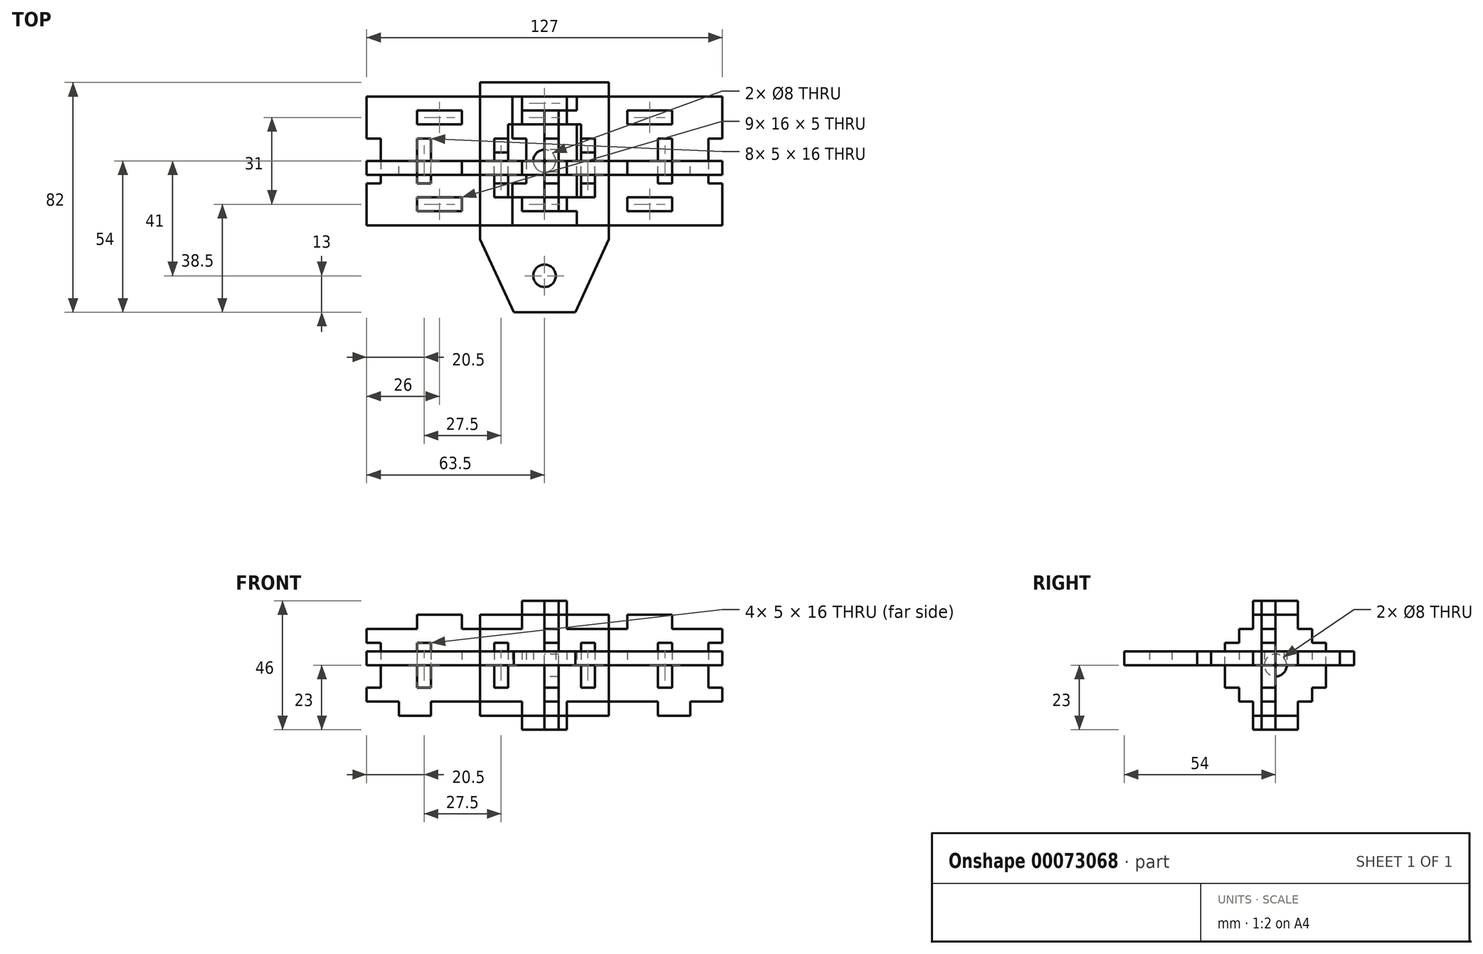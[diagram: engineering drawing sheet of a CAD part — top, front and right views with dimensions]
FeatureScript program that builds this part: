
annotation { "Feature Type Name" : "Feature", "Feature Type Description" : "" }
export const myFeature = defineFeature(function(context is Context, id is Id, definition is map)
    precondition{}
    {
        {
            var Q0;
            Q0=qCreatedBy(makeId("Top.planeOp"),FACE);
            var sketch = newSketch(context, id + "F0", { "sketchPlane" : qUnion([Q0])});
            skLineSegment(sketch, "E0.rect.bottom", {"start": v(63.5, -23) * mm, "end": v(-63.5, -23) * mm});
            skLineSegment(sketch, "E0.rect.top", {"start": v(63.5, 23) * mm, "end": v(-63.5, 23) * mm});
            skLineSegment(sketch, "E0.rect.left", {"start": v(63.5, -23) * mm, "end": v(63.5, -8) * mm});
            skLineSegment(sketch, "E0.rect.right", {"start": v(-63.5, -23) * mm, "end": v(-63.5, -8) * mm});
            skPoint(sketch, "E0.rect.middle", {"position": v(0, 0) * mm});
            skLineSegment(sketch, "E1", {"start": v(-8, -18) * mm, "end": v(8, -18) * mm});
            skLineSegment(sketch, "E2", {"start": v(-63.5, 8) * mm, "end": v(-58.5, 8) * mm});
            skLineSegment(sketch, "E3", {"start": v(-63.5, -8) * mm, "end": v(-58.5, -8) * mm});
            skLineSegment(sketch, "E4", {"start": v(-58.5, 8) * mm, "end": v(-58.5, -8) * mm});
            skLineSegment(sketch, "E5.trimOffspring", {"start": v(-63.5, 8) * mm, "end": v(-63.5, 23) * mm});
            skLineSegment(sketch, "E6", {"start": v(58.5, 8) * mm, "end": v(58.5, -8) * mm});
            skLineSegment(sketch, "E7.trimOffspring", {"start": v(63.5, 8) * mm, "end": v(63.5, 23) * mm});
            skLineSegment(sketch, "E8.rect.bottom", {"start": v(8, -18) * mm, "end": v(-8, -18) * mm});
            skLineSegment(sketch, "E8.rect.top", {"start": v(8, 18) * mm, "end": v(-8, 18) * mm});
            skLineSegment(sketch, "E9.rect.bottom", {"start": v(8, -13) * mm, "end": v(-8, -13) * mm});
            skLineSegment(sketch, "E9.rect.left", {"start": v(18, -8) * mm, "end": v(18, 8) * mm});
            skLineSegment(sketch, "E9.rect.right", {"start": v(-18, -8) * mm, "end": v(-18, 8) * mm});
            skLineSegment(sketch, "E10.rect.left", {"start": v(8, -18) * mm, "end": v(8, -13) * mm});
            skLineSegment(sketch, "E10.rect.right", {"start": v(-8, -18) * mm, "end": v(-8, -13) * mm});
            skLineSegment(sketch, "E11.trimOffspring", {"start": v(-8, 18) * mm, "end": v(8, 18) * mm});
            skLineSegment(sketch, "E12.trimOffspring", {"start": v(-8, 13) * mm, "end": v(-8, 18) * mm});
            skLineSegment(sketch, "E13.trimOffspring", {"start": v(8, 13) * mm, "end": v(8, 18) * mm});
            skLineSegment(sketch, "E14.trimOffspring", {"start": v(8, 13) * mm, "end": v(-8, 13) * mm});
            skLineSegment(sketch, "E15.trimOffspring", {"start": v(13, 8) * mm, "end": v(18, 8) * mm});
            skLineSegment(sketch, "E16.trimOffspring", {"start": v(13, -8) * mm, "end": v(18, -8) * mm});
            skLineSegment(sketch, "E17.trimOffspring", {"start": v(-13, -8) * mm, "end": v(-13, 8) * mm});
            skLineSegment(sketch, "E18.trimOffspring", {"start": v(13, -8) * mm, "end": v(13, 8) * mm});
            skLineSegment(sketch, "E19.trimOffspring", {"start": v(-18, 8) * mm, "end": v(-13, 8) * mm});
            skLineSegment(sketch, "E20.trimOffspring", {"start": v(-18, -8) * mm, "end": v(-13, -8) * mm});
            skLineSegment(sketch, "E21.trimOffspring", {"start": v(58.5, 8) * mm, "end": v(63.5, 8) * mm});
            skLineSegment(sketch, "E22.trimOffspring", {"start": v(58.5, -8) * mm, "end": v(63.5, -8) * mm});
            skLineSegment(sketch, "E23.rect.bottom", {"start": v(-40.5, -8) * mm, "end": v(-45.5, -8) * mm});
            skLineSegment(sketch, "E23.rect.top", {"start": v(-40.5, 8) * mm, "end": v(-45.5, 8) * mm});
            skLineSegment(sketch, "E23.rect.left", {"start": v(-40.5, -8) * mm, "end": v(-40.5, 8) * mm});
            skLineSegment(sketch, "E23.rect.right", {"start": v(-45.5, -8) * mm, "end": v(-45.5, 8) * mm});
            skPoint(sketch, "E23.rect.middle", {"position": v(-43, 0) * mm});
            skLineSegment(sketch, "E24.rect.bottom", {"start": v(45.5, -8) * mm, "end": v(40.5, -8) * mm});
            skLineSegment(sketch, "E24.rect.top", {"start": v(45.5, 8) * mm, "end": v(40.5, 8) * mm});
            skLineSegment(sketch, "E24.rect.left", {"start": v(45.5, -8) * mm, "end": v(45.5, 8) * mm});
            skLineSegment(sketch, "E24.rect.right", {"start": v(40.5, -8) * mm, "end": v(40.5, 8) * mm});
            skPoint(sketch, "E24.rect.middle", {"position": v(43, 0) * mm});
            skLineSegment(sketch, "E25.rect.bottom", {"start": v(-29.5, -18) * mm, "end": v(-45.5, -18) * mm});
            skLineSegment(sketch, "E25.rect.top", {"start": v(-29.5, -13) * mm, "end": v(-45.5, -13) * mm});
            skLineSegment(sketch, "E25.rect.left", {"start": v(-29.5, -18) * mm, "end": v(-29.5, -13) * mm});
            skLineSegment(sketch, "E25.rect.right", {"start": v(-45.5, -18) * mm, "end": v(-45.5, -13) * mm});
            skPoint(sketch, "E25.rect.middle", {"position": v(-37.5, -15.5) * mm});
            skLineSegment(sketch, "E26.rect.bottom", {"start": v(45.5, -18) * mm, "end": v(29.5, -18) * mm});
            skLineSegment(sketch, "E26.rect.top", {"start": v(45.5, -13) * mm, "end": v(29.5, -13) * mm});
            skLineSegment(sketch, "E26.rect.left", {"start": v(45.5, -18) * mm, "end": v(45.5, -13) * mm});
            skLineSegment(sketch, "E26.rect.right", {"start": v(29.5, -18) * mm, "end": v(29.5, -13) * mm});
            skPoint(sketch, "E26.rect.middle", {"position": v(37.5, -15.5) * mm});
            skLineSegment(sketch, "E27.rect.bottom", {"start": v(45.5, 13) * mm, "end": v(29.5, 13) * mm});
            skLineSegment(sketch, "E27.rect.top", {"start": v(45.5, 18) * mm, "end": v(29.5, 18) * mm});
            skLineSegment(sketch, "E27.rect.left", {"start": v(45.5, 13) * mm, "end": v(45.5, 18) * mm});
            skLineSegment(sketch, "E27.rect.right", {"start": v(29.5, 13) * mm, "end": v(29.5, 18) * mm});
            skPoint(sketch, "E27.rect.middle", {"position": v(37.5, 15.5) * mm});
            skLineSegment(sketch, "E28.rect.bottom", {"start": v(-29.5, 13) * mm, "end": v(-45.5, 13) * mm});
            skLineSegment(sketch, "E28.rect.top", {"start": v(-29.5, 18) * mm, "end": v(-45.5, 18) * mm});
            skLineSegment(sketch, "E28.rect.left", {"start": v(-29.5, 13) * mm, "end": v(-29.5, 18) * mm});
            skLineSegment(sketch, "E28.rect.right", {"start": v(-45.5, 13) * mm, "end": v(-45.5, 18) * mm});
            skPoint(sketch, "E28.rect.middle", {"position": v(-37.5, 15.5) * mm});
            skSolve(sketch);
        }
        {
            var Q0;
            Q0=qCreatedBy(makeId("Right.planeOp"),FACE);
            var sketch = newSketch(context, id + "F1", { "sketchPlane" : qUnion([Q0])});
            skLineSegment(sketch, "E29.rect.bottom", {"start": v(18, -8) * mm, "end": v(13, -8) * mm});
            skLineSegment(sketch, "E29.rect.top", {"start": v(18, 8) * mm, "end": v(13, 8) * mm});
            skLineSegment(sketch, "E29.rect.left", {"start": v(18, -8) * mm, "end": v(18, 8) * mm});
            skLineSegment(sketch, "E29.rect.right", {"start": v(-18, -8) * mm, "end": v(-18, 8) * mm});
            skPoint(sketch, "E29.rect.middle", {"position": v(0, 0) * mm});
            skLineSegment(sketch, "E30.rect.bottom", {"start": v(8, -18) * mm, "end": v(-8, -18) * mm});
            skLineSegment(sketch, "E30.rect.top", {"start": v(8, 18) * mm, "end": v(-8, 18) * mm});
            skLineSegment(sketch, "E30.rect.left", {"start": v(8, -18) * mm, "end": v(8, -13) * mm});
            skLineSegment(sketch, "E30.rect.right", {"start": v(-8, -18) * mm, "end": v(-8, -13) * mm});
            skLineSegment(sketch, "E31.rect.bottom", {"start": v(13, -13) * mm, "end": v(8, -13) * mm});
            skLineSegment(sketch, "E31.rect.top", {"start": v(13, 13) * mm, "end": v(8, 13) * mm});
            skLineSegment(sketch, "E31.rect.left", {"start": v(13, -13) * mm, "end": v(13, -8) * mm});
            skLineSegment(sketch, "E31.rect.right", {"start": v(-13, -13) * mm, "end": v(-13, -8) * mm});
            skLineSegment(sketch, "E32.trimOffspring", {"start": v(-8, 13) * mm, "end": v(-13, 13) * mm});
            skLineSegment(sketch, "E33.trimOffspring", {"start": v(-13, 8) * mm, "end": v(-18, 8) * mm});
            skLineSegment(sketch, "E34.trimOffspring", {"start": v(-13, -8) * mm, "end": v(-18, -8) * mm});
            skLineSegment(sketch, "E35.trimOffspring", {"start": v(-8, -13) * mm, "end": v(-13, -13) * mm});
            skLineSegment(sketch, "E36.trimOffspring", {"start": v(-13, 8) * mm, "end": v(-13, 13) * mm});
            skLineSegment(sketch, "E37.trimOffspring", {"start": v(-8, 13) * mm, "end": v(-8, 18) * mm});
            skLineSegment(sketch, "E38.trimOffspring", {"start": v(8, 13) * mm, "end": v(8, 18) * mm});
            skLineSegment(sketch, "E39.trimOffspring", {"start": v(13, 8) * mm, "end": v(13, 13) * mm});
            skCircle(sketch, "E40", {"center": v(0, 0) * mm, "radius": 4 * mm});
            skSolve(sketch);
        }
        {
            var Q0;
            Q0=qCreatedBy(makeId("Top.planeOp"),FACE);
            var sketch = newSketch(context, id + "F2", { "sketchPlane" : qUnion([Q0])});
            skLineSegment(sketch, "E41.rect.bottom", {"start": v(23, -23) * mm, "end": v(-23, -23) * mm});
            skLineSegment(sketch, "E41.rect.top", {"start": v(23, 23) * mm, "end": v(-23, 23) * mm});
            skLineSegment(sketch, "E41.rect.left", {"start": v(23, -23) * mm, "end": v(23, 23) * mm});
            skLineSegment(sketch, "E41.rect.right", {"start": v(-23, -23) * mm, "end": v(-23, 23) * mm});
            skPoint(sketch, "E41.rect.middle", {"position": v(0, 0) * mm});
            skLineSegment(sketch, "E42.rect.bottom", {"start": v(-13, -8) * mm, "end": v(-18, -8) * mm});
            skLineSegment(sketch, "E42.rect.top", {"start": v(-13, 8) * mm, "end": v(-18, 8) * mm});
            skLineSegment(sketch, "E42.rect.left", {"start": v(-13, -8) * mm, "end": v(-13, 8) * mm});
            skLineSegment(sketch, "E42.rect.right", {"start": v(-18, -8) * mm, "end": v(-18, 8) * mm});
            skPoint(sketch, "E42.rect.middle", {"position": v(-15.5, 0) * mm});
            skLineSegment(sketch, "E43.rect.bottom", {"start": v(8, 13) * mm, "end": v(-8, 13) * mm});
            skLineSegment(sketch, "E43.rect.top", {"start": v(8, 18) * mm, "end": v(-8, 18) * mm});
            skLineSegment(sketch, "E43.rect.left", {"start": v(8, 13) * mm, "end": v(8, 18) * mm});
            skLineSegment(sketch, "E43.rect.right", {"start": v(-8, 13) * mm, "end": v(-8, 18) * mm});
            skPoint(sketch, "E43.rect.middle", {"position": v(0, 15.5) * mm});
            skLineSegment(sketch, "E44.rect.bottom", {"start": v(13, -8) * mm, "end": v(18, -8) * mm});
            skLineSegment(sketch, "E44.rect.top", {"start": v(13, 8) * mm, "end": v(18, 8) * mm});
            skLineSegment(sketch, "E44.rect.left", {"start": v(13, -8) * mm, "end": v(13, 8) * mm});
            skLineSegment(sketch, "E44.rect.right", {"start": v(18, -8) * mm, "end": v(18, 8) * mm});
            skPoint(sketch, "E44.rect.middle", {"position": v(15.5, 0) * mm});
            skLineSegment(sketch, "E45.bottom", {"start": v(-8, -13) * mm, "end": v(8, -13) * mm});
            skLineSegment(sketch, "E45.top", {"start": v(-8, -18) * mm, "end": v(8, -18) * mm});
            skLineSegment(sketch, "E45.left", {"start": v(-8, -13) * mm, "end": v(-8, -18) * mm});
            skLineSegment(sketch, "E45.right", {"start": v(8, -13) * mm, "end": v(8, -18) * mm});
            skSolve(sketch);
        }
        {
            var Q0;
            Q0=qCreatedBy(makeId("Top.planeOp"),FACE);
            var sketch = newSketch(context, id + "F3", { "sketchPlane" : qUnion([Q0])});
            skLineSegment(sketch, "E46.rect.bottom", {"start": v(11.5, -23) * mm, "end": v(-11.5, -23) * mm});
            skLineSegment(sketch, "E46.rect.top", {"start": v(11.5, 23) * mm, "end": v(-11.5, 23) * mm});
            skLineSegment(sketch, "E46.rect.left", {"start": v(11.5, -23) * mm, "end": v(11.5, -18) * mm});
            skLineSegment(sketch, "E46.rect.right", {"start": v(-11.5, -23) * mm, "end": v(-11.5, -8) * mm});
            skPoint(sketch, "E46.rect.middle", {"position": v(0, 0) * mm});
            skLineSegment(sketch, "E47", {"start": v(-6.5, 8) * mm, "end": v(-6.5, -8) * mm});
            skLineSegment(sketch, "E48", {"start": v(-11.5, 8) * mm, "end": v(-6.5, 8) * mm});
            skLineSegment(sketch, "E49", {"start": v(-11.5, -8) * mm, "end": v(-6.5, -8) * mm});
            skLineSegment(sketch, "E50.trimOffspring", {"start": v(-11.5, 8) * mm, "end": v(-11.5, 23) * mm});
            skLineSegment(sketch, "E51.bottom", {"start": v(0, 18) * mm, "end": v(11.5, 18) * mm});
            skLineSegment(sketch, "E51.top", {"start": v(0, 13) * mm, "end": v(11.5, 13) * mm});
            skLineSegment(sketch, "E51.left", {"start": v(0, 18) * mm, "end": v(0, 13) * mm});
            skLineSegment(sketch, "E52.trimOffspring", {"start": v(11.5, 18) * mm, "end": v(11.5, 23) * mm});
            skLineSegment(sketch, "E53", {"start": v(11.5, -18) * mm, "end": v(0, -18) * mm});
            skLineSegment(sketch, "E54", {"start": v(0, -18) * mm, "end": v(0, -13) * mm});
            skLineSegment(sketch, "E55", {"start": v(0, -13) * mm, "end": v(11.5, -13) * mm});
            skLineSegment(sketch, "E56.trimOffspring", {"start": v(11.5, -13) * mm, "end": v(11.5, 13) * mm});
            skSolve(sketch);
        }
        {
            var Q0;
            Q0=qCreatedBy(makeId("Front.planeOp"),FACE);
            var sketch = newSketch(context, id + "F4", { "sketchPlane" : qUnion([Q0])});
            skLineSegment(sketch, "E57.rect.bottom", {"start": v(63.5, -13) * mm, "end": v(52, -13) * mm});
            skLineSegment(sketch, "E57.rect.top", {"start": v(63.5, 13) * mm, "end": v(45.5, 13) * mm});
            skLineSegment(sketch, "E57.rect.left", {"start": v(63.5, -13) * mm, "end": v(63.5, -8) * mm});
            skLineSegment(sketch, "E57.rect.right", {"start": v(-63.5, -13) * mm, "end": v(-63.5, -8) * mm});
            skPoint(sketch, "E57.rect.middle", {"position": v(0, 0) * mm});
            skLineSegment(sketch, "E58", {"start": v(-63.5, 8) * mm, "end": v(-58.5, 8) * mm});
            skLineSegment(sketch, "E59", {"start": v(-58.5, 8) * mm, "end": v(-58.5, -8) * mm});
            skLineSegment(sketch, "E60", {"start": v(-58.5, -8) * mm, "end": v(-63.5, -8) * mm});
            skLineSegment(sketch, "E61.trimOffspring", {"start": v(-63.5, 8) * mm, "end": v(-63.5, 13) * mm});
            skLineSegment(sketch, "E62", {"start": v(63.5, 8) * mm, "end": v(58.5, 8) * mm});
            skLineSegment(sketch, "E63", {"start": v(58.5, 8) * mm, "end": v(58.5, -8) * mm});
            skLineSegment(sketch, "E64", {"start": v(58.5, -8) * mm, "end": v(63.5, -8) * mm});
            skLineSegment(sketch, "E65.trimOffspring", {"start": v(63.5, 8) * mm, "end": v(63.5, 13) * mm});
            skLineSegment(sketch, "E66", {"start": v(-8, 13) * mm, "end": v(-8, 18) * mm});
            skLineSegment(sketch, "E67", {"start": v(-8, 18) * mm, "end": v(8, 18) * mm});
            skLineSegment(sketch, "E68", {"start": v(8, 18) * mm, "end": v(8, 13) * mm});
            skLineSegment(sketch, "E69.trimOffspring", {"start": v(-8, 13) * mm, "end": v(-29.5, 13) * mm});
            skLineSegment(sketch, "E70", {"start": v(-8, -13) * mm, "end": v(-8, -18) * mm});
            skLineSegment(sketch, "E71", {"start": v(-8, -18) * mm, "end": v(8, -18) * mm});
            skLineSegment(sketch, "E72", {"start": v(8, -18) * mm, "end": v(8, -13) * mm});
            skLineSegment(sketch, "E73.trimOffspring", {"start": v(-8, -13) * mm, "end": v(-40.5, -13) * mm});
            skLineSegment(sketch, "E74", {"start": v(-45.5, 13) * mm, "end": v(-45.5, 18) * mm});
            skLineSegment(sketch, "E75", {"start": v(-45.5, 18) * mm, "end": v(-29.5, 18) * mm});
            skLineSegment(sketch, "E76", {"start": v(-29.5, 18) * mm, "end": v(-29.5, 13) * mm});
            skLineSegment(sketch, "E77", {"start": v(45.5, 13) * mm, "end": v(45.5, 18) * mm});
            skLineSegment(sketch, "E78", {"start": v(45.5, 18) * mm, "end": v(29.5, 18) * mm});
            skLineSegment(sketch, "E79", {"start": v(29.5, 18) * mm, "end": v(29.5, 13) * mm});
            skLineSegment(sketch, "E80.trimOffspring", {"start": v(-45.5, 13) * mm, "end": v(-63.5, 13) * mm});
            skLineSegment(sketch, "E81.trimOffspring", {"start": v(29.5, 13) * mm, "end": v(8, 13) * mm});
            skLineSegment(sketch, "E82.rect.bottom", {"start": v(-40.5, 8) * mm, "end": v(-45.5, 8) * mm});
            skLineSegment(sketch, "E82.rect.top", {"start": v(-40.5, -8) * mm, "end": v(-45.5, -8) * mm});
            skLineSegment(sketch, "E82.rect.left", {"start": v(-40.5, 8) * mm, "end": v(-40.5, -8) * mm});
            skLineSegment(sketch, "E82.rect.right", {"start": v(-45.5, 8) * mm, "end": v(-45.5, -8) * mm});
            skPoint(sketch, "E82.rect.middle", {"position": v(-43, 0) * mm});
            skLineSegment(sketch, "E83.rect.bottom", {"start": v(-13, 8) * mm, "end": v(-18, 8) * mm});
            skLineSegment(sketch, "E83.rect.top", {"start": v(-13, -8) * mm, "end": v(-18, -8) * mm});
            skLineSegment(sketch, "E83.rect.left", {"start": v(-13, 8) * mm, "end": v(-13, -8) * mm});
            skLineSegment(sketch, "E83.rect.right", {"start": v(-18, 8) * mm, "end": v(-18, -8) * mm});
            skPoint(sketch, "E83.rect.middle", {"position": v(-15.5, 0) * mm});
            skLineSegment(sketch, "E84.rect.bottom", {"start": v(13, 8) * mm, "end": v(18, 8) * mm});
            skLineSegment(sketch, "E84.rect.top", {"start": v(13, -8) * mm, "end": v(18, -8) * mm});
            skLineSegment(sketch, "E84.rect.left", {"start": v(13, 8) * mm, "end": v(13, -8) * mm});
            skLineSegment(sketch, "E84.rect.right", {"start": v(18, 8) * mm, "end": v(18, -8) * mm});
            skPoint(sketch, "E84.rect.middle", {"position": v(15.5, 0) * mm});
            skLineSegment(sketch, "E85.rect.bottom", {"start": v(40.5, 8) * mm, "end": v(45.5, 8) * mm});
            skLineSegment(sketch, "E85.rect.top", {"start": v(40.5, -8) * mm, "end": v(45.5, -8) * mm});
            skLineSegment(sketch, "E85.rect.left", {"start": v(40.5, 8) * mm, "end": v(40.5, -8) * mm});
            skLineSegment(sketch, "E85.rect.right", {"start": v(45.5, 8) * mm, "end": v(45.5, -8) * mm});
            skPoint(sketch, "E85.rect.middle", {"position": v(43, 0) * mm});
            skLineSegment(sketch, "E86", {"start": v(-52, -13) * mm, "end": v(-52, -18) * mm});
            skLineSegment(sketch, "E87", {"start": v(-52, -18) * mm, "end": v(-40.5, -18) * mm});
            skLineSegment(sketch, "E88", {"start": v(-40.5, -18) * mm, "end": v(-40.5, -13) * mm});
            skLineSegment(sketch, "E89.trimOffspring", {"start": v(-52, -13) * mm, "end": v(-63.5, -13) * mm});
            skLineSegment(sketch, "E90", {"start": v(52, -13) * mm, "end": v(52, -18) * mm});
            skLineSegment(sketch, "E91", {"start": v(52, -18) * mm, "end": v(40.5, -18) * mm});
            skLineSegment(sketch, "E92", {"start": v(40.5, -18) * mm, "end": v(40.5, -13) * mm});
            skLineSegment(sketch, "E93.trimOffspring", {"start": v(40.5, -13) * mm, "end": v(8, -13) * mm});
            skSolve(sketch);
        }
        {
            var Q0;
            Q0=qCreatedBy(makeId("Right.planeOp"),FACE);
            var sketch = newSketch(context, id + "F5", { "sketchPlane" : qUnion([Q0])});
            skLineSegment(sketch, "E94.rect.bottom", {"start": v(18, -8) * mm, "end": v(13, -8) * mm});
            skLineSegment(sketch, "E94.rect.top", {"start": v(18, 8) * mm, "end": v(13, 8) * mm});
            skLineSegment(sketch, "E94.rect.left", {"start": v(18, -8) * mm, "end": v(18, 8) * mm});
            skLineSegment(sketch, "E94.rect.right", {"start": v(-18, -8) * mm, "end": v(-18, 8) * mm});
            skPoint(sketch, "E94.rect.middle", {"position": v(0, 0) * mm});
            skLineSegment(sketch, "E95.rect.bottom", {"start": v(8, -18) * mm, "end": v(-8, -18) * mm});
            skLineSegment(sketch, "E95.rect.top", {"start": v(8, 18) * mm, "end": v(-8, 18) * mm});
            skLineSegment(sketch, "E95.rect.left", {"start": v(8, -18) * mm, "end": v(8, -13) * mm});
            skLineSegment(sketch, "E95.rect.right", {"start": v(-8, -18) * mm, "end": v(-8, -13) * mm});
            skLineSegment(sketch, "E96.trimOffspring", {"start": v(-13, 8) * mm, "end": v(-18, 8) * mm});
            skLineSegment(sketch, "E97.trimOffspring", {"start": v(-8, 13) * mm, "end": v(-8, 18) * mm});
            skLineSegment(sketch, "E98.trimOffspring", {"start": v(-13, -8) * mm, "end": v(-18, -8) * mm});
            skLineSegment(sketch, "E99.trimOffspring", {"start": v(8, 13) * mm, "end": v(8, 18) * mm});
            skLineSegment(sketch, "E100.rect.bottom", {"start": v(13, -13) * mm, "end": v(8, -13) * mm});
            skLineSegment(sketch, "E100.rect.top", {"start": v(13, 13) * mm, "end": v(8, 13) * mm});
            skLineSegment(sketch, "E100.rect.left", {"start": v(13, -13) * mm, "end": v(13, -8) * mm});
            skLineSegment(sketch, "E100.rect.right", {"start": v(-13, -13) * mm, "end": v(-13, -8) * mm});
            skLineSegment(sketch, "E101.trimOffspring", {"start": v(-8, 13) * mm, "end": v(-13, 13) * mm});
            skLineSegment(sketch, "E102.trimOffspring", {"start": v(-8, -13) * mm, "end": v(-13, -13) * mm});
            skLineSegment(sketch, "E103.trimOffspring", {"start": v(-13, 8) * mm, "end": v(-13, 13) * mm});
            skLineSegment(sketch, "E104.trimOffspring", {"start": v(13, 8) * mm, "end": v(13, 13) * mm});
            skCircle(sketch, "E105", {"center": v(0, 0) * mm, "radius": 4 * mm});
            skSolve(sketch);
        }
        {
            var Q0;
            Q0=qCreatedBy(makeId("Right.planeOp"),FACE);
            var sketch = newSketch(context, id + "F6", { "sketchPlane" : qUnion([Q0])});
            skLineSegment(sketch, "E106.rect.bottom", {"start": v(18, -8) * mm, "end": v(13, -8) * mm});
            skLineSegment(sketch, "E106.rect.top", {"start": v(18, 8) * mm, "end": v(13, 8) * mm});
            skLineSegment(sketch, "E106.rect.left", {"start": v(18, -8) * mm, "end": v(18, 8) * mm});
            skLineSegment(sketch, "E106.rect.right", {"start": v(-18, -8) * mm, "end": v(-18, 8) * mm});
            skPoint(sketch, "E106.rect.middle", {"position": v(0, 0) * mm});
            skLineSegment(sketch, "E107.rect.bottom", {"start": v(8, -23) * mm, "end": v(-8, -23) * mm});
            skLineSegment(sketch, "E107.rect.top", {"start": v(8, 23) * mm, "end": v(-8, 23) * mm});
            skLineSegment(sketch, "E107.rect.left", {"start": v(8, -23) * mm, "end": v(8, -13) * mm});
            skLineSegment(sketch, "E107.rect.right", {"start": v(-8, -23) * mm, "end": v(-8, -13) * mm});
            skLineSegment(sketch, "E108.rect.bottom", {"start": v(13, -13) * mm, "end": v(8, -13) * mm});
            skLineSegment(sketch, "E108.rect.top", {"start": v(13, 13) * mm, "end": v(8, 13) * mm});
            skLineSegment(sketch, "E108.rect.left", {"start": v(13, -13) * mm, "end": v(13, -8) * mm});
            skLineSegment(sketch, "E108.rect.right", {"start": v(-13, -13) * mm, "end": v(-13, -8) * mm});
            skLineSegment(sketch, "E109.trimOffspring", {"start": v(-8, 13) * mm, "end": v(-13, 13) * mm});
            skLineSegment(sketch, "E110.trimOffspring", {"start": v(-13, 8) * mm, "end": v(-18, 8) * mm});
            skLineSegment(sketch, "E111.trimOffspring", {"start": v(-13, -8) * mm, "end": v(-18, -8) * mm});
            skLineSegment(sketch, "E112.trimOffspring", {"start": v(-8, -13) * mm, "end": v(-13, -13) * mm});
            skLineSegment(sketch, "E113.trimOffspring", {"start": v(-13, 8) * mm, "end": v(-13, 13) * mm});
            skLineSegment(sketch, "E114.trimOffspring", {"start": v(-8, 13) * mm, "end": v(-8, 23) * mm});
            skLineSegment(sketch, "E115.trimOffspring", {"start": v(8, 13) * mm, "end": v(8, 23) * mm});
            skLineSegment(sketch, "E116.trimOffspring", {"start": v(13, 8) * mm, "end": v(13, 13) * mm});
            skSolve(sketch);
        }
        {
            var Q0;
            Q0=qCreatedBy(makeId("Top.planeOp"),FACE);
            var sketch = newSketch(context, id + "F7", { "sketchPlane" : qUnion([Q0])});
            skLineSegment(sketch, "E117.rect.bottom", {"start": v(23, -28) * mm, "end": v(-23, -28) * mm, "construction": true});
            skLineSegment(sketch, "E117.rect.top", {"start": v(23, 28) * mm, "end": v(-23, 28) * mm});
            skLineSegment(sketch, "E117.rect.left", {"start": v(23, -28) * mm, "end": v(23, 28) * mm});
            skLineSegment(sketch, "E117.rect.right", {"start": v(-23, -28) * mm, "end": v(-23, 28) * mm});
            skPoint(sketch, "E117.rect.middle", {"position": v(0, 0) * mm});
            skLineSegment(sketch, "E118", {"start": v(-23, -28) * mm, "end": v(-11, -54) * mm});
            skLineSegment(sketch, "E119", {"start": v(-11, -54) * mm, "end": v(11, -54) * mm});
            skLineSegment(sketch, "E120", {"start": v(11, -54) * mm, "end": v(23, -28) * mm});
            skCircle(sketch, "E121", {"center": v(0, -41) * mm, "radius": 4 * mm});
            skLineSegment(sketch, "E122", {"start": v(-18, -13) * mm, "end": v(-13, -13) * mm});
            skLineSegment(sketch, "E123", {"start": v(-18, -13) * mm, "end": v(-18, 3) * mm});
            skLineSegment(sketch, "E124", {"start": v(-18, 3) * mm, "end": v(-13, 3) * mm});
            skLineSegment(sketch, "E125", {"start": v(-13, 3) * mm, "end": v(-13, -13) * mm});
            skLineSegment(sketch, "E126", {"start": v(-13, -13) * mm, "end": v(-18, -13) * mm});
            skLineSegment(sketch, "E127", {"start": v(-8, 23) * mm, "end": v(8, 23) * mm});
            skLineSegment(sketch, "E128", {"start": v(8, 23) * mm, "end": v(8, 18) * mm});
            skLineSegment(sketch, "E129", {"start": v(8, 18) * mm, "end": v(-8, 18) * mm});
            skLineSegment(sketch, "E130", {"start": v(-8, 18) * mm, "end": v(-8, 23) * mm});
            skLineSegment(sketch, "E131", {"start": v(13, 3) * mm, "end": v(13, -13) * mm});
            skLineSegment(sketch, "E132", {"start": v(13, -13) * mm, "end": v(18, -13) * mm});
            skLineSegment(sketch, "E133", {"start": v(18, -13) * mm, "end": v(18, 3) * mm});
            skLineSegment(sketch, "E134", {"start": v(18, 3) * mm, "end": v(13, 3) * mm});
            skSolve(sketch);
        }
        {
            var Q0;
            Q0=qCreatedBy(makeId("Front.planeOp"),FACE);
            var sketch = newSketch(context, id + "F8", { "sketchPlane" : qUnion([Q0])});
            skLineSegment(sketch, "E135.rect.bottom", {"start": v(8, -23) * mm, "end": v(-8, -23) * mm});
            skLineSegment(sketch, "E135.rect.top", {"start": v(8, 23) * mm, "end": v(-8, 23) * mm});
            skLineSegment(sketch, "E135.rect.left", {"start": v(8, -23) * mm, "end": v(8, -18) * mm});
            skLineSegment(sketch, "E135.rect.right", {"start": v(-8, -23) * mm, "end": v(-8, -18) * mm});
            skPoint(sketch, "E135.rect.middle", {"position": v(0, 0) * mm});
            skLineSegment(sketch, "E136.rect.bottom", {"start": v(23, -18) * mm, "end": v(8, -18) * mm});
            skLineSegment(sketch, "E136.rect.top", {"start": v(23, 18) * mm, "end": v(8, 18) * mm});
            skLineSegment(sketch, "E136.rect.left", {"start": v(23, -18) * mm, "end": v(23, 18) * mm});
            skLineSegment(sketch, "E136.rect.right", {"start": v(-23, -18) * mm, "end": v(-23, 18) * mm});
            skLineSegment(sketch, "E137.trimOffspring", {"start": v(-8, 18) * mm, "end": v(-23, 18) * mm});
            skLineSegment(sketch, "E138.trimOffspring", {"start": v(8, 18) * mm, "end": v(8, 23) * mm});
            skLineSegment(sketch, "E139.trimOffspring", {"start": v(-8, 18) * mm, "end": v(-8, 23) * mm});
            skLineSegment(sketch, "E140.trimOffspring", {"start": v(-8, -18) * mm, "end": v(-23, -18) * mm});
            skSolve(sketch);
        }
        {
            var Q0;
            Q0 = qSketchRegion(id + "F0", true);
            extrude(context, id + "F9", {"entities" : qUnion([Q0]), "depth" : 5 * mm});
        }
        {
            var Q0;
            Q0=makeQuery(id+"F1.imprint","IMPRINT",FACE,{"disambiguationData":[TD([[makeQuery(id+"F1.imprint","IMPRINT",EDGE,{"derivedFrom":sQuery(id+"F1.wireOp",EDGE,"E29.rect.bottom")}),-1.0]])]});
            extrude(context, id + "F10", {"entities" : qUnion([Q0]), "depth" : 5 * mm});
        }
        {
            var Q0;
            Q0=makeQuery(id+"F2.imprint","IMPRINT",FACE,{"disambiguationData":[TD([[makeQuery(id+"F2.imprint","IMPRINT",EDGE,{"derivedFrom":sQuery(id+"F2.wireOp",EDGE,"E41.rect.bottom")}),-1.0]])]});
            extrude(context, id + "F11", {"entities" : qUnion([Q0]), "depth" : 5 * mm});
        }
        {
            var Q0;
            Q0 = qSketchRegion(id + "F3", true);
            var Q1;
            Q1=makeQuery(id+"F3.imprint","IMPRINT",FACE,{"disambiguationData":[TD([[makeQuery(id+"F3.imprint","IMPRINT",EDGE,{"derivedFrom":sQuery(id+"F3.wireOp",EDGE,"E46.rect.bottom")}),-1.0]])]});
            extrude(context, id + "F12", {"entities" : qUnion([Q0, Q1]), "depth" : 5 * mm});
        }
        {
            var Q0;
            Q0=makeQuery(id+"F4.imprint","IMPRINT",FACE,{"disambiguationData":[TD([[makeQuery(id+"F4.imprint","IMPRINT",EDGE,{"derivedFrom":sQuery(id+"F4.wireOp",EDGE,"E57.rect.bottom")}),-1.0]])]});
            extrude(context, id + "F13", {"entities" : qUnion([Q0]), "depth" : 5 * mm});
        }
        {
            var Q0;
            Q0=makeQuery(id+"F5.imprint","IMPRINT",FACE,{"disambiguationData":[TD([[makeQuery(id+"F5.imprint","IMPRINT",EDGE,{"derivedFrom":sQuery(id+"F5.wireOp",EDGE,"E94.rect.bottom")}),-1.0]])]});
            extrude(context, id + "F14", {"entities" : qUnion([Q0]), "depth" : 5 * mm});
        }
        {
            var Q0;
            Q0 = qSketchRegion(id + "F6", true);
            var Q1;
            Q1=makeQuery(id+"F6.imprint","IMPRINT",FACE,{"disambiguationData":[TD([[makeQuery(id+"F6.imprint","IMPRINT",EDGE,{"derivedFrom":sQuery(id+"F6.wireOp",EDGE,"E106.rect.bottom")}),-1.0]])]});
            extrude(context, id + "F15", {"entities" : qUnion([Q0, Q1]), "depth" : 5 * mm});
        }
        {
            var Q0;
            Q0=makeQuery(id+"F7.imprint","IMPRINT",FACE,{"disambiguationData":[TD([[makeQuery(id+"F7.imprint","IMPRINT",EDGE,{"derivedFrom":sQuery(id+"F7.wireOp",EDGE,"E117.rect.top")}),1.0]])]});
            extrude(context, id + "F16", {"entities" : qUnion([Q0]), "depth" : 5 * mm});
        }
        {
            var Q0;
            Q0=makeQuery(id+"F8.imprint","IMPRINT",FACE,{"disambiguationData":[TD([[makeQuery(id+"F8.imprint","IMPRINT",EDGE,{"derivedFrom":sQuery(id+"F8.wireOp",EDGE,"E135.rect.bottom")}),-1.0]])]});
            extrude(context, id + "F17", {"entities" : qUnion([Q0]), "depth" : 5 * mm});
        }
        {
            var Q0;
            Q0=qCreatedBy(makeId("Top.planeOp"),FACE);
            var sketch = newSketch(context, id + "F18", { "sketchPlane" : qUnion([Q0])});
            skLineSegment(sketch, "E141.rect.bottom", {"start": v(13, -13) * mm, "end": v(-13, -13) * mm});
            skLineSegment(sketch, "E141.rect.top", {"start": v(13, 13) * mm, "end": v(-13, 13) * mm});
            skLineSegment(sketch, "E141.rect.left", {"start": v(13, -13) * mm, "end": v(13, 13) * mm});
            skLineSegment(sketch, "E141.rect.right", {"start": v(-13, -13) * mm, "end": v(-13, 13) * mm});
            skPoint(sketch, "E141.rect.middle", {"position": v(0, 0) * mm});
            skCircle(sketch, "E142", {"center": v(0, 0) * mm, "radius": 4 * mm});
            skSolve(sketch);
        }
        {
            var Q0;
            Q0 = qSketchRegion(id + "F18", true);
            var Q1;
            Q1=makeQuery(id+"F18.imprint","IMPRINT",FACE,{"disambiguationData":[TD([[makeQuery(id+"F18.imprint","IMPRINT",EDGE,{"derivedFrom":sQuery(id+"F18.wireOp",EDGE,"E141.rect.bottom")}),-1.0]])]});
            extrude(context, id + "F19", {"entities" : qUnion([Q0, Q1]), "depth" : 5 * mm});
        }
    });
